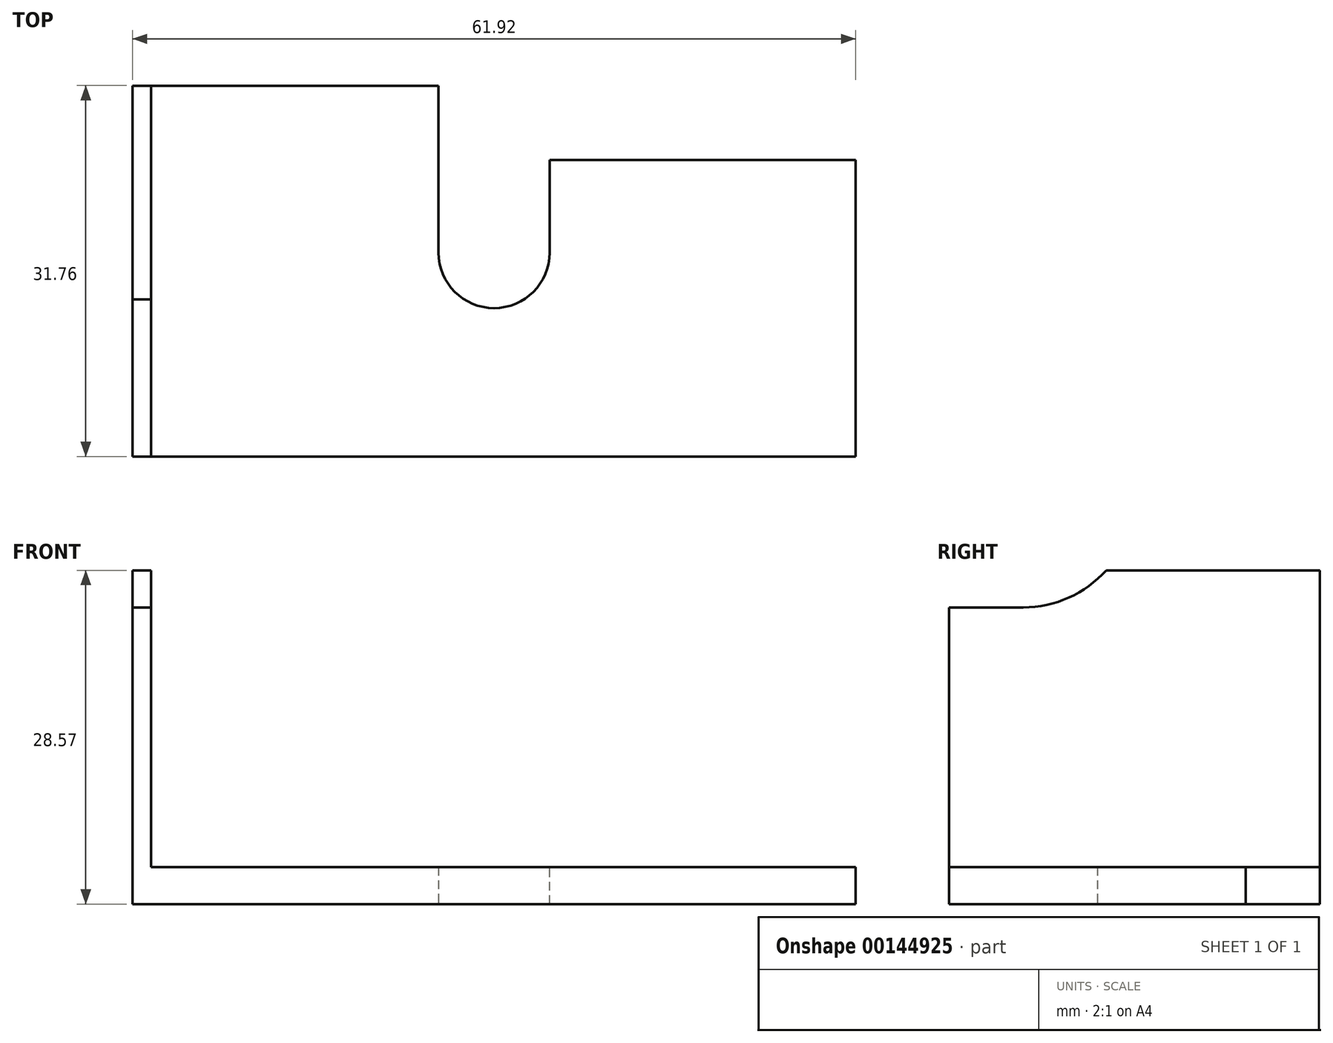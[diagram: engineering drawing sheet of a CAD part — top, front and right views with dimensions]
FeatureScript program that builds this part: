
annotation { "Feature Type Name" : "Feature", "Feature Type Description" : "" }
export const myFeature = defineFeature(function(context is Context, id is Id, definition is map)
    precondition{}
    {
        {
            var Q0;
            Q0=qCreatedBy(makeId("Top.planeOp"),FACE);
            var sketch = newSketch(context, id + "F0", { "sketchPlane" : qUnion([Q0])});
            skLineSegment(sketch, "E0.bottom", {"start": v(30.96, 15.88) * mm, "end": v(-30.96, 15.88) * mm});
            skLineSegment(sketch, "E0.top", {"start": v(30.96, -15.88) * mm, "end": v(-30.96, -15.88) * mm});
            skLineSegment(sketch, "E0.left", {"start": v(30.96, 15.88) * mm, "end": v(30.96, -15.88) * mm});
            skLineSegment(sketch, "E0.right", {"start": v(-30.96, 15.88) * mm, "end": v(-30.96, -15.87) * mm});
            skPoint(sketch, "E0.middle", {"position": v(0, 0) * mm});
            skCircle(sketch, "E1", {"center": v(0, 1.59) * mm, "radius": 4.76 * mm});
            skPoint(sketch, "E1.centerSnap0", {"position": v(0, -15.88) * mm});
            skLineSegment(sketch, "E2.bottom", {"start": v(-4.76, 1.59) * mm, "end": v(4.76, 1.59) * mm});
            skLineSegment(sketch, "E2.top", {"start": v(-4.76, 15.88) * mm, "end": v(4.76, 15.88) * mm});
            skLineSegment(sketch, "E2.left", {"start": v(-4.76, 1.59) * mm, "end": v(-4.76, 15.88) * mm});
            skLineSegment(sketch, "E2.right", {"start": v(4.76, 1.59) * mm, "end": v(4.76, 15.88) * mm});
            skSolve(sketch);
        }
        {
            var Q0;
            Q0=makeQuery(id+"F0.imprint","IMPRINT",FACE,{"disambiguationData":[TD([[makeQuery(id+"F0.imprint","IMPRINT",EDGE,{"derivedFrom":sQuery(id+"F0.wireOp",EDGE,"E0.top")}),-1.0]])]});
            extrude(context, id + "F1", {"entities" : qUnion([Q0]), "depth" : 3.17 * mm});
        }
        {
            var Q0;
            Q0=makeQuery(id+"F1.opExtrude","CAP_FACE",FACE,{"disambiguationData":[OSD([sQuery(id+"F0.wireOp",EDGE,"E0.bottom"),sQuery(id+"F0.wireOp",EDGE,"E0.top"),sQuery(id+"F0.wireOp",EDGE,"E0.left"),sQuery(id+"F0.wireOp",EDGE,"E0.right"),sQuery(id+"F0.wireOp",EDGE,"E1"),sQuery(id+"F0.wireOp",EDGE,"E2.left"),sQuery(id+"F0.wireOp",EDGE,"E2.right")])],"isStart":false});
            var sketch = newSketch(context, id + "F2", { "sketchPlane" : qUnion([Q0])});
            skLineSegment(sketch, "E3.bottom", {"start": v(-30.96, -15.87) * mm, "end": v(-29.37, -15.87) * mm});
            skLineSegment(sketch, "E3.top", {"start": v(-30.96, 15.88) * mm, "end": v(-29.37, 15.88) * mm});
            skLineSegment(sketch, "E3.left", {"start": v(-30.96, -15.88) * mm, "end": v(-30.96, 15.88) * mm});
            skLineSegment(sketch, "E3.right", {"start": v(-29.37, -15.87) * mm, "end": v(-29.37, 15.88) * mm});
            skSolve(sketch);
        }
        {
            var Q0;
            Q0=makeQuery(id+"F2.imprint","IMPRINT",FACE,{"disambiguationData":[TD([[makeQuery(id+"F2.imprint","IMPRINT",EDGE,{"derivedFrom":sQuery(id+"F2.wireOp",EDGE,"E3.bottom")}),-1.0]])]});
            extrude(context, id + "F3", {"entities" : qUnion([Q0]), "operationType" : NewBodyOperationType.ADD, "depth" : 25.4 * mm});
        }
        {
            var Q0;
            Q0=makeQuery(id+"F3.boolean.opBoolean","MERGE",FACE,{"derivedFrom":[makeQuery(id+"F1.opExtrude","SWEPT_FACE",FACE,{"disambiguationData":[OSD([sQuery(id+"F0.wireOp",EDGE,"E0.right")])]}),makeQuery(id+"F3.opExtrude","SWEPT_FACE",FACE,{"disambiguationData":[OSD([sQuery(id+"F2.wireOp",EDGE,"E3.left")])]})]});
            var sketch = newSketch(context, id + "F4", { "sketchPlane" : qUnion([Q0])});
            skCircle(sketch, "E4", {"center": v(9.52, 34.93) * mm, "radius": 9.53 * mm});
            skLineSegment(sketch, "E5.bottom", {"start": v(9.52, 44.45) * mm, "end": v(22.8, 44.45) * mm});
            skLineSegment(sketch, "E5.top", {"start": v(9.52, 25.4) * mm, "end": v(22.8, 25.4) * mm});
            skLineSegment(sketch, "E5.left", {"start": v(9.52, 44.45) * mm, "end": v(9.52, 25.4) * mm});
            skLineSegment(sketch, "E5.right", {"start": v(22.8, 44.45) * mm, "end": v(22.8, 25.4) * mm});
            skSolve(sketch);
        }
        {
            var Q0;
            {var subQ1=sQuery(id+"F4.wireOp",EDGE,"E4");var subQ3=makeQuery(id+"F3.opExtrude","CAP_EDGE",EDGE,{"disambiguationData":[OSD([sQuery(id+"F2.wireOp",EDGE,"E3.left")])],"isStart":false});var subQ4=makeQuery(id+"F4.imprint","INTERSECT",VERTEX,{"derivedFrom":[subQ3,subQ1]});Q0=makeQuery(id+"F4.imprint","IMPRINT",FACE,{"disambiguationData":[TD([[makeQuery(id+"F4.imprint","IMPRINT",EDGE,{"disambiguationData":[TD([[subQ4,-1.0]])],"derivedFrom":subQ3}),-1.0]])]});}
            var Q1;
            {var subQ0=sQuery(id+"F4.wireOp",EDGE,"E5.left");var subQ3=sQuery(id+"F2.wireOp",EDGE,"E3.left");var subQ6=makeQuery(id+"F3.opExtrude","CAP_EDGE",EDGE,{"disambiguationData":[OSD([subQ3])],"isStart":false});var subQ7=makeQuery(id+"F4.imprint","INTERSECT",VERTEX,{"derivedFrom":[subQ6,subQ0]});Q1=makeQuery(id+"F4.imprint","IMPRINT",FACE,{"disambiguationData":[TD([[makeQuery(id+"F4.imprint","IMPRINT",EDGE,{"disambiguationData":[TD([[subQ7,-1.0]])],"derivedFrom":subQ0}),1.0]])]});}
            var Q2;
            {var subQ0=sQuery(id+"F4.wireOp",EDGE,"E5.top");var subQ1=sQuery(id+"F4.wireOp",EDGE,"E4");var subQ2=makeQuery(id+"F4.imprint","INTERSECT",VERTEX,{"derivedFrom":[subQ1,subQ0,sQuery(id+"F4.wireOp",EDGE,"E5.left")]});Q2=makeQuery(id+"F4.imprint","IMPRINT",FACE,{"disambiguationData":[TD([[makeQuery(id+"F4.imprint","IMPRINT",EDGE,{"disambiguationData":[TD([[subQ2,-1.0]])],"derivedFrom":subQ1}),-1.0]])]});}
            extrude(context, id + "F5", {"entities" : qUnion([Q0, Q1, Q2]), "operationType" : NewBodyOperationType.REMOVE, "oppositeDirection" : true, "depth" : 25.4 * mm});
        }
        {
            var Q0;
            Q0=makeQuery(id+"F1.opExtrude","CAP_FACE",FACE,{"disambiguationData":[OSD([sQuery(id+"F0.wireOp",EDGE,"E0.bottom"),sQuery(id+"F0.wireOp",EDGE,"E0.top"),sQuery(id+"F0.wireOp",EDGE,"E0.left"),sQuery(id+"F0.wireOp",EDGE,"E0.right"),sQuery(id+"F0.wireOp",EDGE,"E1"),sQuery(id+"F0.wireOp",EDGE,"E2.left"),sQuery(id+"F0.wireOp",EDGE,"E2.right")])],"isStart":false});
            var sketch = newSketch(context, id + "F6", { "sketchPlane" : qUnion([Q0])});
            skLineSegment(sketch, "E6.bottom", {"start": v(4.76, 15.88) * mm, "end": v(30.96, 15.88) * mm});
            skLineSegment(sketch, "E6.top", {"start": v(4.76, 9.53) * mm, "end": v(30.96, 9.53) * mm});
            skLineSegment(sketch, "E6.left", {"start": v(4.76, 15.88) * mm, "end": v(4.76, 9.53) * mm});
            skLineSegment(sketch, "E6.right", {"start": v(30.96, 15.88) * mm, "end": v(30.96, 9.53) * mm});
            skSolve(sketch);
        }
        {
            var Q0;
            Q0=makeQuery(id+"F6.imprint","IMPRINT",FACE,{"disambiguationData":[TD([[makeQuery(id+"F6.imprint","IMPRINT",EDGE,{"derivedFrom":sQuery(id+"F6.wireOp",EDGE,"E6.bottom")}),1.0]])]});
            extrude(context, id + "F7", {"entities" : qUnion([Q0]), "operationType" : NewBodyOperationType.REMOVE, "oppositeDirection" : true, "depth" : 25.4 * mm});
        }
    });
